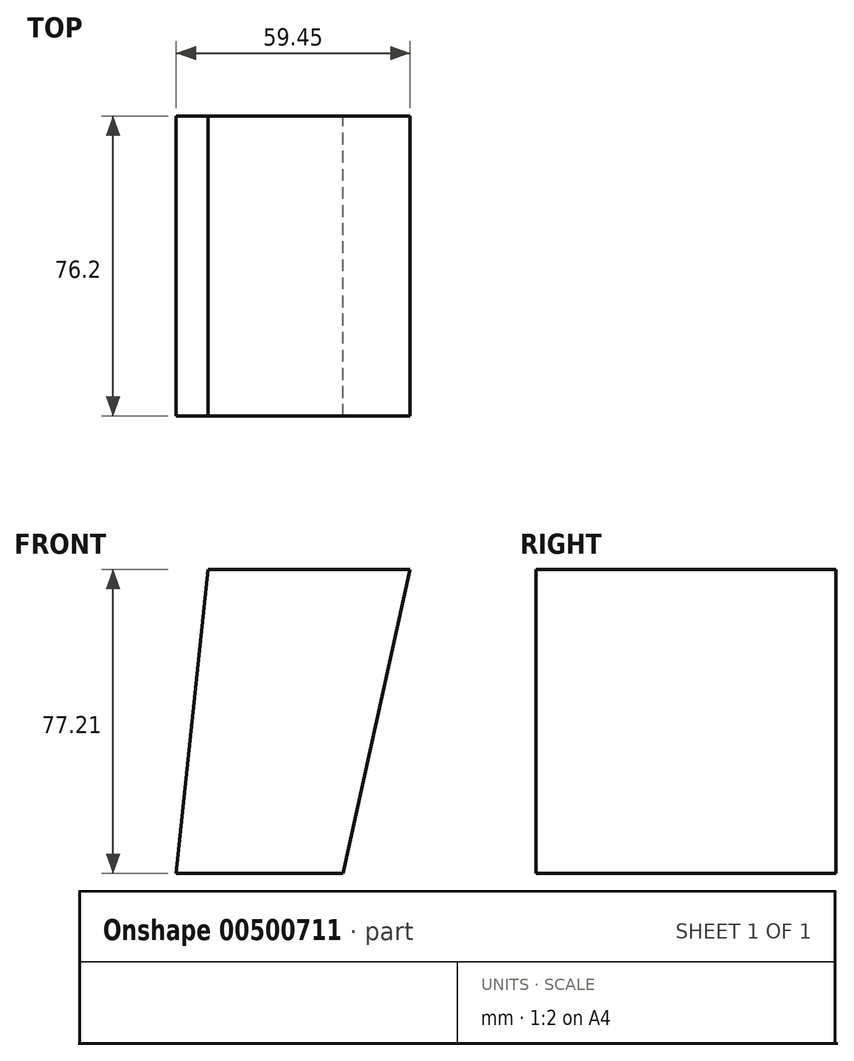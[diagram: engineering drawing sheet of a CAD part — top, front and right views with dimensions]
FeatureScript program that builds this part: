
annotation { "Feature Type Name" : "Feature", "Feature Type Description" : "" }
export const myFeature = defineFeature(function(context is Context, id is Id, definition is map)
    precondition{}
    {
        {
            var Q0;
            Q0=qCreatedBy(makeId("Front.planeOp"),FACE);
            var sketch = newSketch(context, id + "F0", { "sketchPlane" : qUnion([Q0])});
            skLineSegment(sketch, "E0.top", {"start": v(-56.46, 15.52) * mm, "end": v(-14.04, 15.52) * mm});
            skLineSegment(sketch, "E1", {"start": v(-48.38, 92.73) * mm, "end": v(2.99, 92.73) * mm});
            skLineSegment(sketch, "E2", {"start": v(-48.38, 92.73) * mm, "end": v(-56.46, 15.52) * mm});
            skLineSegment(sketch, "E3", {"start": v(2.99, 92.73) * mm, "end": v(-14.04, 15.52) * mm});
            skLineSegment(sketch, "E4", {"start": v(-48.38, 92.73) * mm, "end": v(-48.38, 15.52) * mm});
            skLineSegment(sketch, "E5", {"start": v(-14.04, 15.52) * mm, "end": v(-14.04, 92.73) * mm});
            skSolve(sketch);
        }
        {
            var Q0;
            {var subQ2=sQuery(id+"F0.wireOp",EDGE,"E4");Q0=makeQuery(id+"F0.imprint","IMPRINT",FACE,{"disambiguationData":[TD([[makeQuery(id+"F0.imprint","IMPRINT",EDGE,{"derivedFrom":subQ2}),1.0]])]});}
            var Q1;
            {var subQ0=sQuery(id+"F0.wireOp",EDGE,"E3");Q1=makeQuery(id+"F0.imprint","IMPRINT",FACE,{"disambiguationData":[TD([[makeQuery(id+"F0.imprint","IMPRINT",EDGE,{"derivedFrom":subQ0}),-1.0]])]});}
            var Q2;
            {var subQ0=sQuery(id+"F0.wireOp",EDGE,"E2");Q2=makeQuery(id+"F0.imprint","IMPRINT",FACE,{"disambiguationData":[TD([[makeQuery(id+"F0.imprint","IMPRINT",EDGE,{"derivedFrom":subQ0}),1.0]])]});}
            extrude(context, id + "F1", {"entities" : qUnion([Q0, Q1, Q2]), "depth" : 76.2 * mm});
        }
    });
